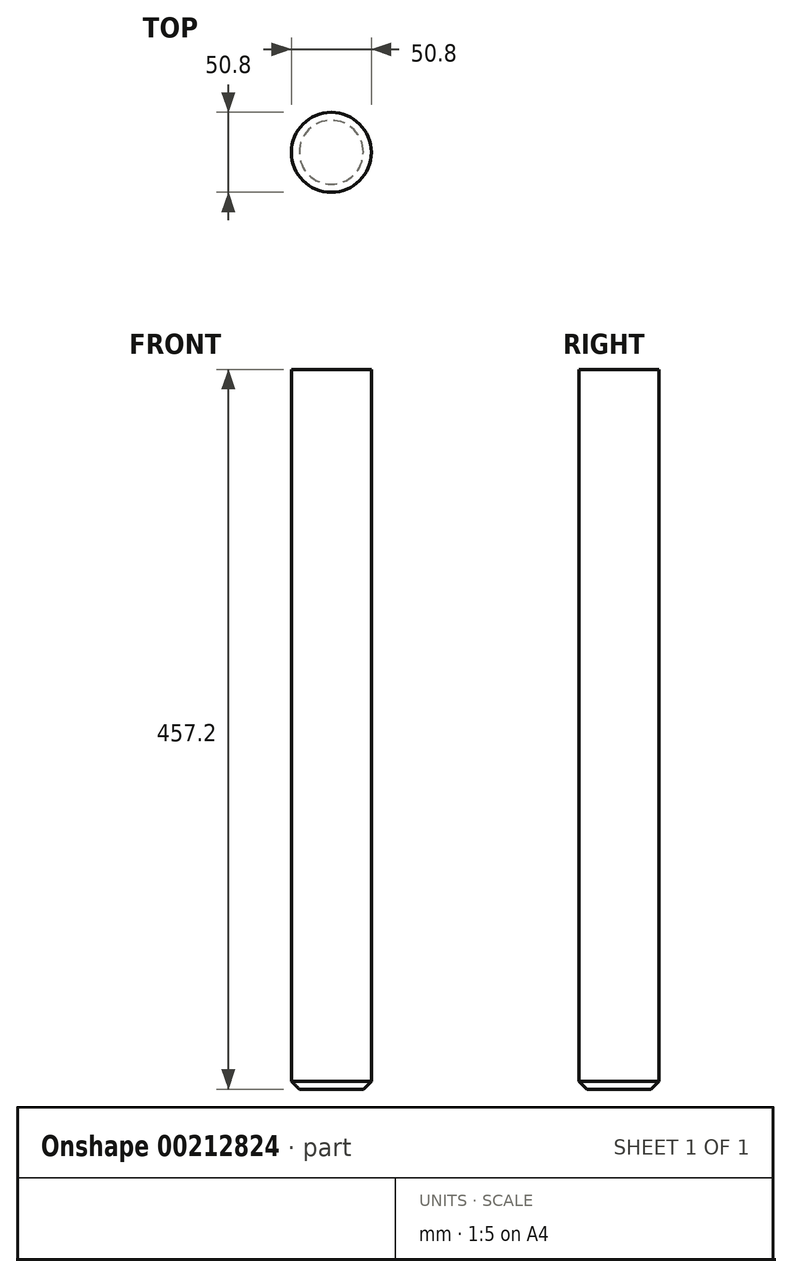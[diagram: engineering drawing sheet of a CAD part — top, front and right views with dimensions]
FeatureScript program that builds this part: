
annotation { "Feature Type Name" : "Feature", "Feature Type Description" : "" }
export const myFeature = defineFeature(function(context is Context, id is Id, definition is map)
    precondition{}
    {
        {
            var Q0;
            Q0=qCreatedBy(makeId("Front.planeOp"),FACE);
            var sketch = newSketch(context, id + "F0", { "sketchPlane" : qUnion([Q0])});
            skLineSegment(sketch, "E0.bottom", {"start": v(25.4, 228.6) * mm, "end": v(-25.4, 228.6) * mm});
            skLineSegment(sketch, "E0.top", {"start": v(25.4, -228.6) * mm, "end": v(-25.4, -228.6) * mm});
            skLineSegment(sketch, "E0.left", {"start": v(25.4, 228.6) * mm, "end": v(25.4, -228.6) * mm});
            skLineSegment(sketch, "E0.right", {"start": v(-25.4, 228.6) * mm, "end": v(-25.4, -228.6) * mm});
            skPoint(sketch, "E0.middle", {"position": v(0, 0) * mm});
            skLineSegment(sketch, "E1", {"start": v(0, 228.6) * mm, "end": v(0, -228.6) * mm});
            skSolve(sketch);
        }
        {
            var Q0;
            {var subQ0=sQuery(id+"F0.wireOp",EDGE,"E0.left");Q0=makeQuery(id+"F0.imprint","IMPRINT",FACE,{"disambiguationData":[TD([[makeQuery(id+"F0.imprint","IMPRINT",EDGE,{"derivedFrom":subQ0}),-1.0]])]});}
            var Q1;
            Q1=sQuery(id+"F0.wireOp",EDGE,"E1");
            revolve(context, id + "F1", {"entities" : qUnion([Q0]), "axis" : qUnion([Q1]), "revolveType" : RevolveType.FULL});
        }
        {
            var Q0;
            Q0=makeQuery(id+"F1.opRevolve","SWEPT_FACE",FACE,{"disambiguationData":[OSD([sQuery(id+"F0.wireOp",EDGE,"E0.top")])]});
            chamfer(context, id + "F2", {"entities" : qUnion([Q0]), "width" : 5.08 * mm, "tangentPropagation" : true});
        }
    });
